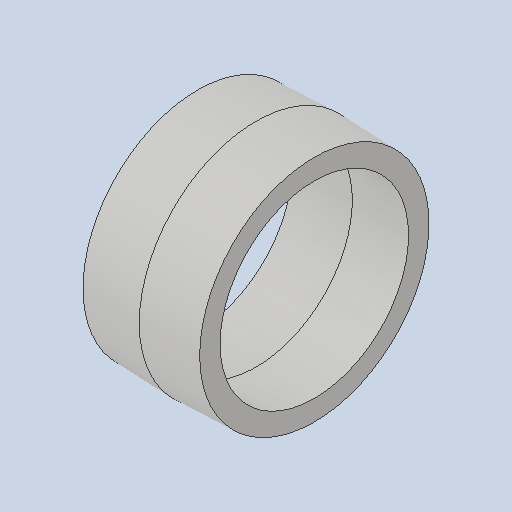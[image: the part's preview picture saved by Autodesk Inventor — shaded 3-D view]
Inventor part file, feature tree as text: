
AUTODESK INVENTOR PART (.ipt)
format: ipt  version: 2023 (Build 270158000, 158)  size: 107,520 bytes
history: native  units: in
note: dims shown in document units (in); Inventor stores cm internally (conversion verified against a paired STEP export)
features: revolve x1
ambient origin geometry x8: Origin, YZ Plane, XZ Plane, XY Plane, X Axis, Y Axis, Z Axis, Center Point
bodies: Solid1 (feature_tree)
feature tree (1):
  revolve  "Revolve1"  [1 undecoded]
note: 1 required parameter value undecoded (feature->parameter linkage not recoverable at this tier; creation-order binding heuristic only, values carry confidence <= 0.55)
